# Revit family: Naughtone_Stng_Hatch_Bench1
name_source: partatom
category: Furniture
revit_build: Autodesk Revit 2015 (Build: 20160512_1515(x64)
units: mm (PartAtom-declared; Revit-internal decimal feet)

## types (3) — shared parameters
Assembly Code = E2020200
AssetType = Movable
BIMObjectName = Naughtone_Seating_Hatch_Bench
CodePerformance = PASSED BSEN 16139
Color = Various
DurationUnit = year
Finish = Upholstered
IfcExportAs = IfcFurnishingElementType
MainColor = Various
ManufacturerAddressUK = naughtone, Knaresborough Tech Park, Manse Lane, Knaresborough, HG5 8LF
ManufacturerName = Naughtone
ManufacturerURL = www.naughtone.com
Material = Fabric, leather/steel/solid wood/beech ply/foam
NBSDescription = Seating
NBSReference = 45-35-72/352
Name = Seating_Hatch_Bench_Naughtone
NominalHeight = 410 mm  [stored 1.34514 ft]
NominalWidth = 510 mm  [stored 1.67323 ft]
ProductInformation = www.naughtone.com/portfolio-view/hatch
SustainabilityPerformance = FSC certified. FISP certified. ISO 14001 certified
URL = www.naughtone.com
Uniclass2015Version = Products v1.5
Version = 1
WarrantyDurationLabor = 5
WarrantyDurationParts = 5
WarrantyDurationUnit = year

## per-type parameters (varying)
| type | Category | Description | IfcExportType | Is2Seat | Is3Seat | IsChair | Keynote | LeftOffset | ModelReference | NominalLength | RightOffset | Shape | Size | Uniclass2015Description | Uniclass2015Reference | VoidOffset2Seat | VoidOffset3Seat | VoidOffsetCentre |
| HAT1ST | Pr_40_50_12_85: Stools | Hatch Single Stool | STOOL | No | No | No | Pr_40_50_12_85 | 255 mm  [stored 0.836614 ft] | Hatch Single Stool | 510 mm  [stored 1.67323 ft] | 255 mm  [stored 0.836614 ft] | Square | 510x510x410mm | Stools | Pr_40_50_12_85 | 10 mm  [stored 0.0328084 ft] | 10 mm  [stored 0.0328084 ft] | 255 mm  [stored 0.836614 ft] |
| HAT2BEN | Pr_40_50_12_07: Benches | Hatch 2 Seat Bench | BENCH | Yes | No | Yes | Pr_40_50_12_07 | 510 mm  [stored 1.67323 ft] | Hatch 2 Seat Bench | 1020 mm  [stored 3.34646 ft] | 510 mm  [stored 1.67323 ft] | Rectangular | 1020x510x410mm | Benches | Pr_40_50_12_07 | 0 mm  [stored 0 ft] | 10 mm  [stored 0.0328084 ft] | 0 mm  [stored 0 ft] |
| HAT3BEN | Pr_40_50_12_07: Benches | Hatch 3 Seat Bench | BENCH | Yes | Yes | No | Pr_40_50_12_07 | 765 mm  [stored 2.50984 ft] | Hatch 3 Seat Bench | 1530 mm  [stored 5.01969 ft] | 765 mm  [stored 2.50984 ft] | Rectangular | 1530x510x410mm | Benches | Pr_40_50_12_07 | 0 mm  [stored 0 ft] | 0 mm  [stored 0 ft] | 255 mm  [stored 0.836614 ft] |

note: column(s) folded — value = type name in every type: Model, ModelNumber

note: [stored X ft] marks values corroborated as IEEE doubles in the binary element streams (Revit-internal decimal feet)

## geometry (parser evidence)
native form markers: Sweep x5
no freeform markers — native parametric forms only
